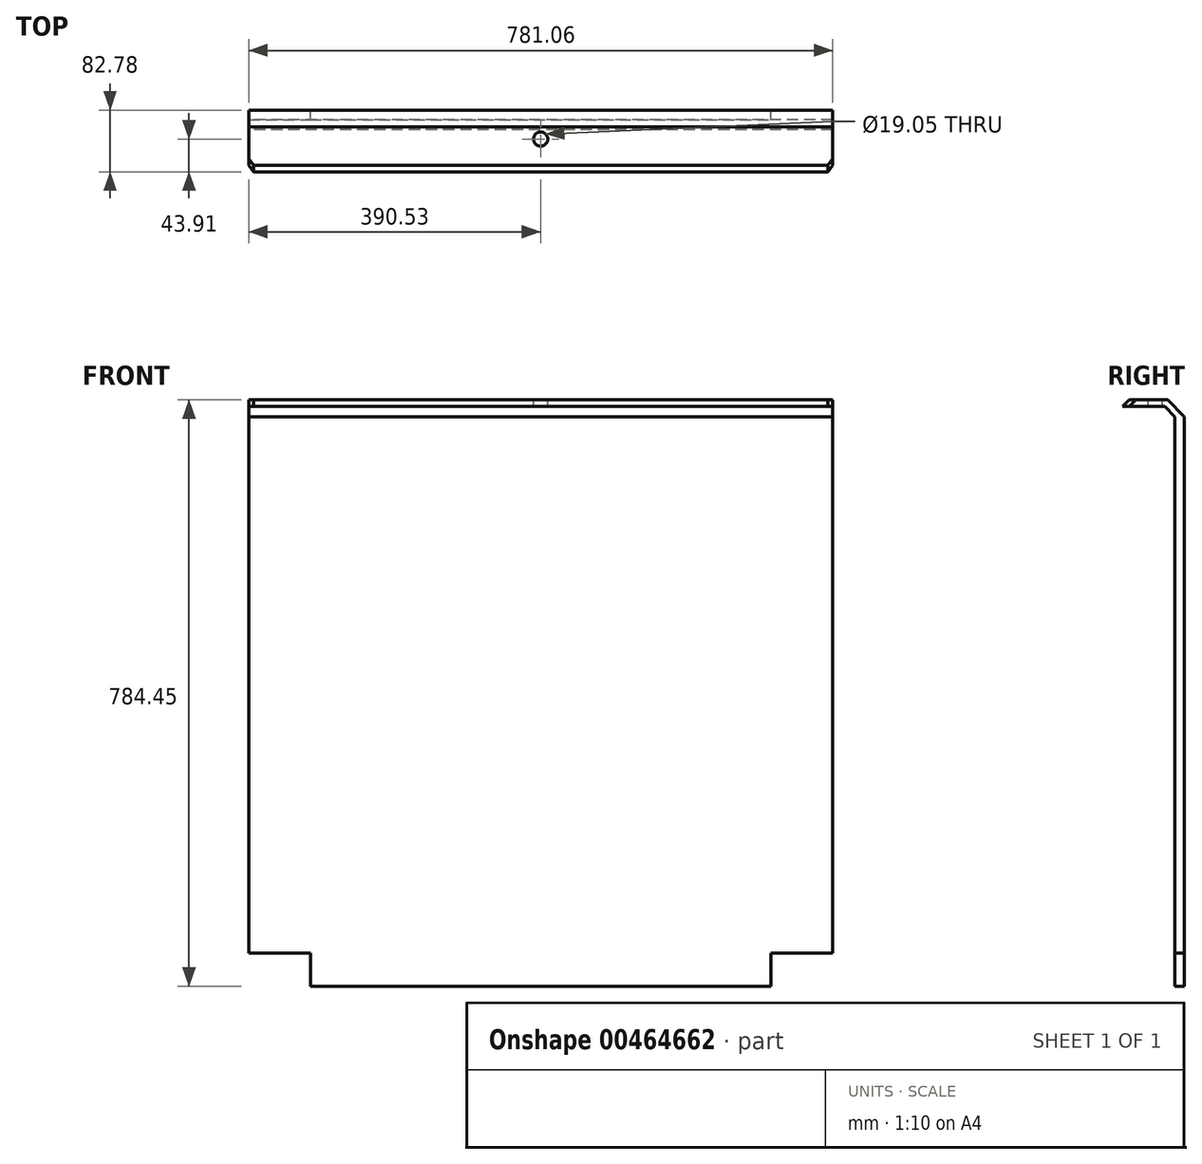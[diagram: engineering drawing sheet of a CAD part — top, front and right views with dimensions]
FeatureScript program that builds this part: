
annotation { "Feature Type Name" : "Feature", "Feature Type Description" : "" }
export const myFeature = defineFeature(function(context is Context, id is Id, definition is map)
    precondition{}
    {
        {
            var Q0;
            Q0=qCreatedBy(makeId("Front.planeOp"),FACE);
            var sketch = newSketch(context, id + "F0", { "sketchPlane" : qUnion([Q0])});
            skLineSegment(sketch, "E0", {"start": v(-307.98, -381) * mm, "end": v(307.98, -381) * mm});
            skLineSegment(sketch, "E1", {"start": v(390.53, -336.55) * mm, "end": v(390.53, 381) * mm});
            skLineSegment(sketch, "E2", {"start": v(390.53, 381) * mm, "end": v(-390.53, 381) * mm});
            skLineSegment(sketch, "E3", {"start": v(-390.53, 381) * mm, "end": v(-390.53, -336.55) * mm});
            skLineSegment(sketch, "E4", {"start": v(-390.53, -336.55) * mm, "end": v(-307.98, -336.55) * mm});
            skLineSegment(sketch, "E5", {"start": v(-307.98, -336.55) * mm, "end": v(-307.98, -381) * mm});
            skLineSegment(sketch, "E6.MirrorCS", {"start": v(390.53, -336.55) * mm, "end": v(307.98, -336.55) * mm});
            skLineSegment(sketch, "E7.MirrorCS", {"start": v(307.98, -336.55) * mm, "end": v(307.98, -381) * mm});
            skPoint(sketch, "E8.orphan", {"position": v(-390.53, -381) * mm});
            skSolve(sketch);
        }
        {
            var Q0;
            Q0=makeQuery(id+"F0.imprint","IMPRINT",FACE,{"disambiguationData":[TD([[makeQuery(id+"F0.imprint","IMPRINT",EDGE,{"derivedFrom":sQuery(id+"F0.wireOp",EDGE,"E0")}),1.0]])]});
            extrude(context, id + "F1", {"entities" : qUnion([Q0]), "depth" : 12.7 * mm, "offsetDistance" : 25.4 * mm});
        }
        {
            var Q0;
            Q0=makeQuery(id+"F1.opExtrude","SWEPT_FACE",FACE,{"disambiguationData":[OSD([sQuery(id+"F0.wireOp",EDGE,"E3")])]});
            var sketch = newSketch(context, id + "F2", { "sketchPlane" : qUnion([Q0])});
            skLineSegment(sketch, "E9", {"start": v(6.35, 381) * mm, "end": v(24.31, 398.96) * mm});
            skLineSegment(sketch, "E10", {"start": v(24.31, 398.96) * mm, "end": v(78.29, 398.96) * mm});
            skSolve(sketch);
        }
        {
            var Q0;
            Q0=makeQuery(id+"F1.opExtrude","SWEPT_FACE",FACE,{"disambiguationData":[OSD([sQuery(id+"F0.wireOp",EDGE,"E2")])]});
            var Q1;
            Q1=sQuery(id+"F2.wireOp",EDGE,"E9");
            var Q2;
            Q2=sQuery(id+"F2.wireOp",EDGE,"E10");
            sweep(context, id + "F3", {"operationType" : NewBodyOperationType.ADD, "profiles" : qUnion([Q0]), "path" : qUnion([Q1, Q2])});
        }
        {
            var Q0;
            Q0=makeQuery(id+"F3.opSweep","CAP_EDGE",EDGE,{"disambiguationData":[OSD([sQuery(id+"F0.wireOp",EDGE,"E2"),sQuery(id+"F0.wireOp",EDGE,"E3"),sQuery(id+"F2.wireOp",VERTEX,"E10.end")])],"isStart":false});
            var Q1;
            Q1=makeQuery(id+"F3.opSweep","CAP_EDGE",EDGE,{"disambiguationData":[OSD([sQuery(id+"F0.wireOp",EDGE,"E1"),sQuery(id+"F0.wireOp",EDGE,"E2"),sQuery(id+"F2.wireOp",VERTEX,"E10.end")])],"isStart":false});
            chamfer(context, id + "F4", {"entities" : qUnion([Q0, Q1]), "width" : 6.35 * mm, "tangentPropagation" : true});
        }
        {
            var Q0;
            {var subQ0=sQuery(id+"F2.wireOp",EDGE,"E10");var subQ1=sQuery(id+"F0.wireOp",EDGE,"E2");Q0=makeQuery(id+"F3.opSweep","SWEPT_FACE",FACE,{"disambiguationData":[OSD([subQ1,subQ0]),TDD([makeQuery(id+"F1.opExtrude","CAP_EDGE",EDGE,{"disambiguationData":[OSD([subQ1])],"isStart":true}),subQ0])]});}
            var sketch = newSketch(context, id + "F5", { "sketchPlane" : qUnion([Q0])});
            skLineSegment(sketch, "E11", {"start": v(0, -73.8) * mm, "end": v(0, -38.87) * mm});
            skSolve(sketch);
        }
        {
            var Q0;
            Q0=sQuery(id+"F5.wireOp",VERTEX,"E11.end");
            var Q1;
            Q1=makeQuery(id+"F1.opExtrude","SWEPT_BODY",BODY,{"disambiguationData":[OSD([sQuery(id+"F0.wireOp",EDGE,"E0"),sQuery(id+"F0.wireOp",EDGE,"E1"),sQuery(id+"F0.wireOp",EDGE,"E2"),sQuery(id+"F0.wireOp",EDGE,"E3"),sQuery(id+"F0.wireOp",EDGE,"E4"),sQuery(id+"F0.wireOp",EDGE,"E5"),sQuery(id+"F0.wireOp",EDGE,"E6.MirrorCS"),sQuery(id+"F0.wireOp",EDGE,"E7.MirrorCS")])]});
            hole(context, id + "F6", {"style" : HoleStyle.SIMPLE, "endStyle" : HoleEndStyle.BLIND, "holeDiameter" : 19.05 * mm, "holeDepth" : 1524 * mm, "locations" : qUnion([Q0]), "scope" : qUnion([Q1])});
        }
    });
